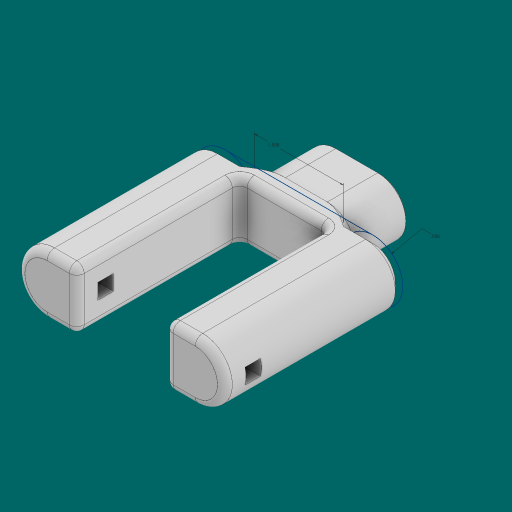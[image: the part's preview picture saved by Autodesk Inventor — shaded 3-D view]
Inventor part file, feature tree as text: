
AUTODESK INVENTOR PART (.ipt)
format: ipt  version: 2023.1 (Build 271208000, 208)  size: 238,080 bytes
history: native  units: in
note: dims shown in document units (in); Inventor stores cm internally (conversion verified against a paired STEP export)
features: extrude x4, sketch x3, fillet x3, chamfer x3
ambient origin geometry x8: Origin, YZ Plane, XZ Plane, XY Plane, X Axis, Y Axis, Z Axis, Center Point
bodies: Solid1 (feature_tree)
feature tree (13):
  extrude  "Extrusion1"  Depth=0.25in TaperAngle=0.0deg
  sketch  "Sketch2"  dims[d4=3.0in d5=0.0in d6=0.26in]
  extrude  "Extrusion2"  Depth=0.26in
  extrude  "Extrusion3"  TaperAngle=0.0deg  [1 undecoded]
  extrude  "Extrusion4"  Depth=0.4724in
  fillet  "Fillet1"  Radius=0.4724in
  fillet  "Fillet2"  Radius=0.7087in
  fillet  "Fillet3"  Radius=1.5in
  chamfer  "Chamfer1"  Distance=0.125in
  chamfer  "Chamfer2"  Distance=0.125in
  chamfer  "Chamfer3"  Distance=0.125in
  sketch  "Sketch1"  dims[d0=1.0in d1=0.0in d2=0.25in d3=0.0in]
  sketch  "Sketch3"  dims[d7=0.26in d8=0.0in d9=0.0in d10=0.5in d11=0.4724in d12=0.7087in d13=1.5in d14=0.125in d15=0.125in d16=0.125in d17=0.125in d18=0.125in d19=45.0deg d20=0.125in d21=0.125in d22=45.0deg d23=0.0236in d24=0.125in d25=45.0deg]
note: 1 required parameter value undecoded (feature->parameter linkage not recoverable at this tier; creation-order binding heuristic only, values carry confidence <= 0.55)
